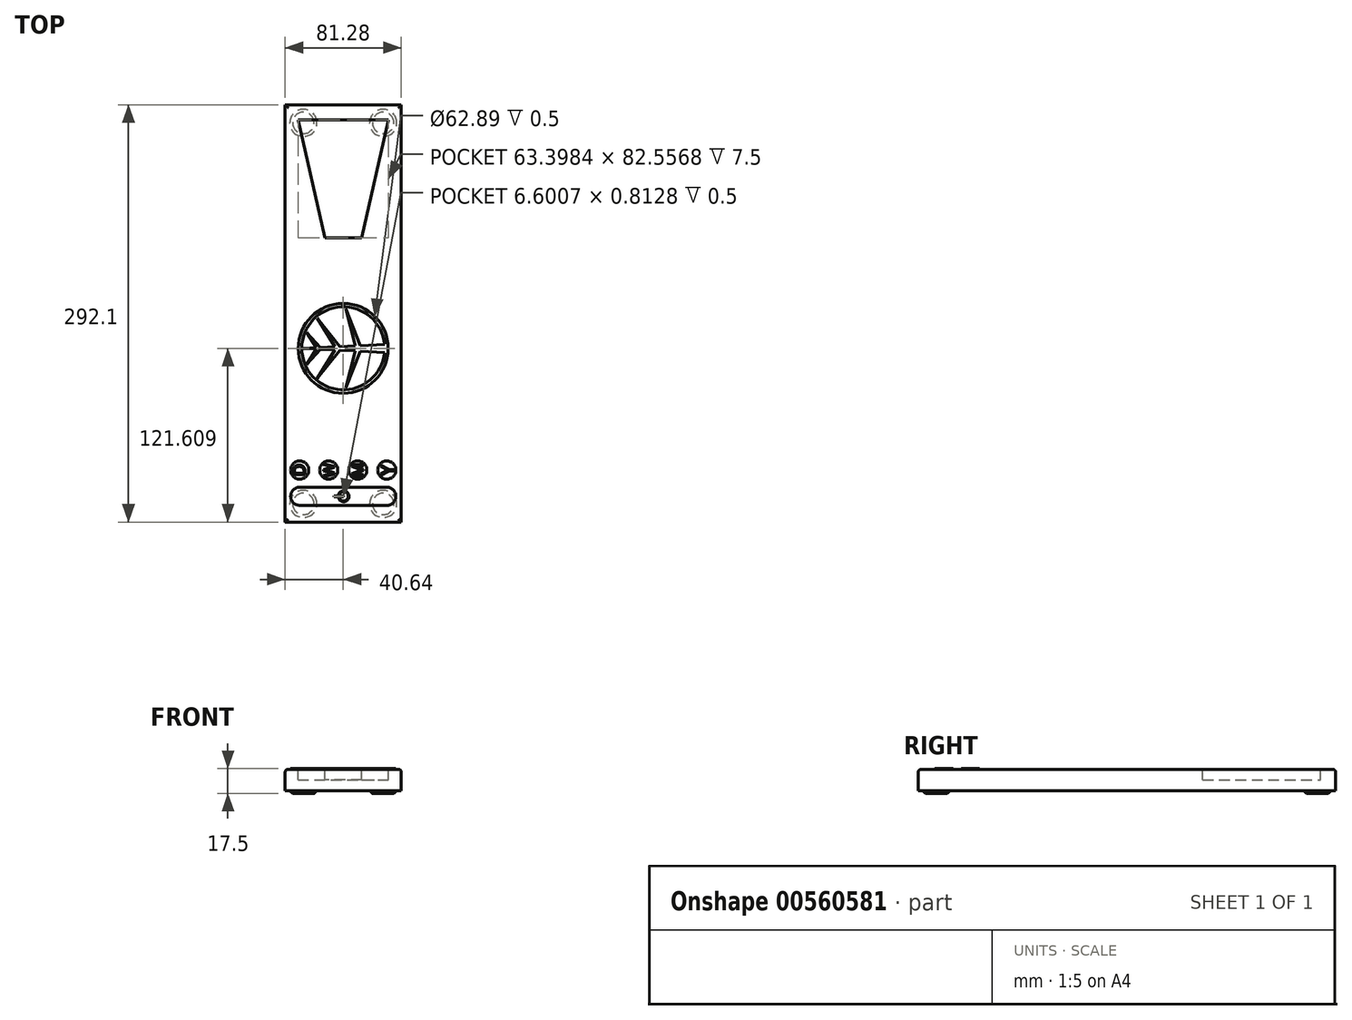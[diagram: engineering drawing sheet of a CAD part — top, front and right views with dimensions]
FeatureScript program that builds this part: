
annotation { "Feature Type Name" : "Feature", "Feature Type Description" : "" }
export const myFeature = defineFeature(function(context is Context, id is Id, definition is map)
    precondition{}
    {
        {
            var Q0;
            Q0=qCreatedBy(makeId("Right.planeOp"),FACE);
            var sketch = newSketch(context, id + "F0", { "sketchPlane" : qUnion([Q0])});
            skLineSegment(sketch, "E0.bottom", {"start": v(-151.29, 3.86) * mm, "end": v(140.81, 3.86) * mm});
            skLineSegment(sketch, "E0.top", {"start": v(-151.29, -11.14) * mm, "end": v(140.81, -11.14) * mm});
            skLineSegment(sketch, "E0.left", {"start": v(-151.29, 3.86) * mm, "end": v(-151.29, -11.14) * mm});
            skLineSegment(sketch, "E0.right", {"start": v(140.81, 3.86) * mm, "end": v(140.81, -11.14) * mm});
            skSolve(sketch);
        }
        {
            var Q0;
            Q0=makeQuery(id+"F0.imprint","IMPRINT",FACE,{"disambiguationData":[TD([[makeQuery(id+"F0.imprint","IMPRINT",EDGE,{"derivedFrom":sQuery(id+"F0.wireOp",EDGE,"E0.bottom")}),-1.0]])]});
            extrude(context, id + "F1", {"entities" : qUnion([Q0]), "depth" : 81.28 * mm, "offsetDistance" : 25.4 * mm});
        }
        {
            var Q0;
            Q0=makeQuery(id+"F1.opExtrude","SWEPT_FACE",FACE,{"disambiguationData":[OSD([sQuery(id+"F0.wireOp",EDGE,"E0.bottom")])]});
            var sketch = newSketch(context, id + "F2", { "sketchPlane" : qUnion([Q0])});
            skLineSegment(sketch, "E1", {"start": v(40.64, 130.27) * mm, "end": v(72.34, 130.27) * mm});
            skPoint(sketch, "E1.startSnap0", {"position": v(40.64, 140.81) * mm});
            skLineSegment(sketch, "E2", {"start": v(40.64, 130.27) * mm, "end": v(8.94, 130.27) * mm});
            skLineSegment(sketch, "E3", {"start": v(40.64, 47.71) * mm, "end": v(27.69, 47.71) * mm});
            skLineSegment(sketch, "E4", {"start": v(27.69, 47.71) * mm, "end": v(40.64, 47.71) * mm});
            skLineSegment(sketch, "E5", {"start": v(53.6, 47.71) * mm, "end": v(40.64, 47.71) * mm});
            skLineSegment(sketch, "E6", {"start": v(53.6, 47.71) * mm, "end": v(72.34, 130.27) * mm});
            skLineSegment(sketch, "E7", {"start": v(8.94, 130.27) * mm, "end": v(27.69, 47.71) * mm});
            skSolve(sketch);
        }
        {
            var Q0;
            Q0=makeQuery(id+"F2.imprint","IMPRINT",FACE,{"disambiguationData":[TD([[makeQuery(id+"F2.imprint","IMPRINT",EDGE,{"derivedFrom":sQuery(id+"F2.wireOp",EDGE,"E1")}),-1.0]])]});
            extrude(context, id + "F3", {"entities" : qUnion([Q0]), "operationType" : NewBodyOperationType.REMOVE, "oppositeDirection" : true, "depth" : 7.5 * mm, "offsetDistance" : 25.4 * mm});
        }
        {
            var Q0;
            Q0=makeQuery(id+"F1.opExtrude","SWEPT_FACE",FACE,{"disambiguationData":[OSD([sQuery(id+"F0.wireOp",EDGE,"E0.bottom")])]});
            var sketch = newSketch(context, id + "F4", { "sketchPlane" : qUnion([Q0])});
            skCircle(sketch, "E8", {"center": v(10.16, -114.9) * mm, "radius": 6.35 * mm});
            skCircle(sketch, "E9", {"center": v(30.48, -114.9) * mm, "radius": 6.35 * mm});
            skCircle(sketch, "E10", {"center": v(50.8, -114.9) * mm, "radius": 6.35 * mm});
            skCircle(sketch, "E11", {"center": v(71.12, -114.9) * mm, "radius": 6.35 * mm});
            skLineSegment(sketch, "E12", {"start": v(10.16, -114.9) * mm, "end": v(30.48, -114.9) * mm, "construction": true});
            skLineSegment(sketch, "E13", {"start": v(71.12, -114.9) * mm, "end": v(50.8, -114.9) * mm, "construction": true});
            skLineSegment(sketch, "E14", {"start": v(30.48, -114.9) * mm, "end": v(50.8, -114.9) * mm, "construction": true});
            skLineSegment(sketch, "E15.bottom", {"start": v(10.27, -126.9) * mm, "end": v(71.48, -126.9) * mm});
            skLineSegment(sketch, "E15.top", {"start": v(10.68, -139.58) * mm, "end": v(71.5, -139.58) * mm});
            skArc(sketch, "E16", {"start": v(10.27, -126.9) * mm, "mid": v(3.81, -133.45) * mm, "end": v(10.68, -139.58) * mm});
            skArc(sketch, "E17", {"start": v(71.5, -139.58) * mm, "mid": v(77.47, -133.23) * mm, "end": v(71.48, -126.9) * mm});
            skSolve(sketch);
        }
        {
            var Q0;
            Q0 = qSketchRegion(id + "F4", true);
            extrude(context, id + "F5", {"entities" : qUnion([Q0]), "operationType" : NewBodyOperationType.ADD, "depth" : .5 * mm, "offsetDistance" : 25.4 * mm});
        }
        {
            var Q0;
            Q0=makeQuery(id+"F5.opExtrude","CAP_FACE",FACE,{"disambiguationData":[OSD([sQuery(id+"F4.wireOp",EDGE,"E8")])],"isStart":false});
            var sketch = newSketch(context, id + "F6", { "sketchPlane" : qUnion([Q0])});
            skText(sketch, "E18", { "text": "D", "fontName": "OpenSans-Regular.ttf"});
            const initialGuessF6  = {"E18": [0.01393, -0.11922, 0, 1, 0.00842]};
            skSetInitialGuess(sketch, initialGuessF6);
            skSolve(sketch);
        }
        {
            var Q0;
            Q0 = qSketchRegion(id + "F6", true);
            extrude(context, id + "F7", {"entities" : qUnion([Q0]), "operationType" : NewBodyOperationType.REMOVE, "oppositeDirection" : true, "depth" : .5 * mm, "offsetDistance" : 25.4 * mm});
        }
        {
            var Q0;
            Q0=makeQuery(id+"F5.opExtrude","CAP_FACE",FACE,{"disambiguationData":[OSD([sQuery(id+"F4.wireOp",EDGE,"E9")])],"isStart":false});
            var sketch = newSketch(context, id + "F8", { "sketchPlane" : qUnion([Q0])});
            skText(sketch, "E19", { "text": "W", "fontName": "OpenSans-Regular.ttf"});
            const initialGuessF8  = {"E19": [0.03434, -0.1197, 0, 1, 0.00744]};
            skSetInitialGuess(sketch, initialGuessF8);
            skSolve(sketch);
        }
        {
            var Q0;
            Q0 = qSketchRegion(id + "F8", true);
            extrude(context, id + "F9", {"entities" : qUnion([Q0]), "operationType" : NewBodyOperationType.REMOVE, "oppositeDirection" : true, "depth" : .5 * mm, "offsetDistance" : 25.4 * mm});
        }
        {
            var Q0;
            Q0=makeQuery(id+"F5.opExtrude","CAP_FACE",FACE,{"disambiguationData":[OSD([sQuery(id+"F4.wireOp",EDGE,"E10")])],"isStart":false});
            var sketch = newSketch(context, id + "F10", { "sketchPlane" : qUnion([Q0])});
            skText(sketch, "E20", { "text": "M", "fontName": "OpenSans-Regular.ttf"});
            const initialGuessF10  = {"E20": [0.05468, -0.11996, 0, 1, 0.00807]};
            skSetInitialGuess(sketch, initialGuessF10);
            skSolve(sketch);
        }
        {
            var Q0;
            Q0 = qSketchRegion(id + "F10", true);
            extrude(context, id + "F11", {"entities" : qUnion([Q0]), "operationType" : NewBodyOperationType.REMOVE, "oppositeDirection" : true, "depth" : .5 * mm, "offsetDistance" : 25.4 * mm});
        }
        {
            var Q0;
            Q0=makeQuery(id+"F5.opExtrude","CAP_FACE",FACE,{"disambiguationData":[OSD([sQuery(id+"F4.wireOp",EDGE,"E11")])],"isStart":false});
            var sketch = newSketch(context, id + "F12", { "sketchPlane" : qUnion([Q0])});
            skText(sketch, "E21", { "text": "Y", "fontName": "OpenSans-Regular.ttf"});
            const initialGuessF12  = {"E21": [0.07649, -0.1187, 0, 1, 0.00957]};
            skSetInitialGuess(sketch, initialGuessF12);
            skSolve(sketch);
        }
        {
            var Q0;
            Q0 = qSketchRegion(id + "F12", true);
            extrude(context, id + "F13", {"entities" : qUnion([Q0]), "operationType" : NewBodyOperationType.REMOVE, "oppositeDirection" : true, "depth" : .5 * mm, "offsetDistance" : 25.4 * mm});
        }
        {
            var Q0;
            Q0=makeQuery(id+"F5.opExtrude","CAP_FACE",FACE,{"disambiguationData":[OSD([sQuery(id+"F4.wireOp",EDGE,"E15.bottom"),sQuery(id+"F4.wireOp",EDGE,"E15.top"),sQuery(id+"F4.wireOp",EDGE,"E16"),sQuery(id+"F4.wireOp",EDGE,"E17")])],"isStart":false});
            var sketch = newSketch(context, id + "F14", { "sketchPlane" : qUnion([Q0])});
            skArc(sketch, "E22", {"start": v(37.35, -134.68) * mm, "mid": v(44.68, -133.17) * mm, "end": v(37.3, -131.93) * mm});
            skPoint(sketch, "E23", {"position": v(40.87, -126.9) * mm});
            skArc(sketch, "E24", {"start": v(37.87, -134.46) * mm, "mid": v(44.12, -133.18) * mm, "end": v(37.83, -132.13) * mm});
            skLineSegment(sketch, "E25", {"start": v(37.3, -131.93) * mm, "end": v(37.83, -132.13) * mm});
            skLineSegment(sketch, "E26", {"start": v(37.35, -134.68) * mm, "end": v(37.87, -134.46) * mm});
            skLineSegment(sketch, "E27.bottom", {"start": v(40.87, -132.89) * mm, "end": v(34.27, -132.89) * mm});
            skLineSegment(sketch, "E27.top", {"start": v(40.87, -133.7) * mm, "end": v(34.27, -133.7) * mm});
            skLineSegment(sketch, "E27.left", {"start": v(40.87, -132.89) * mm, "end": v(40.87, -133.7) * mm});
            skLineSegment(sketch, "E27.right", {"start": v(34.27, -132.89) * mm, "end": v(34.27, -133.7) * mm});
            skPoint(sketch, "E27.middle", {"position": v(37.57, -133.3) * mm});
            skPoint(sketch, "E28.orphan", {"position": v(34.27, -133.35) * mm});
            skSolve(sketch);
        }
        {
            var Q0;
            Q0=makeQuery(id+"F14.imprint","IMPRINT",FACE,{"disambiguationData":[TD([[makeQuery(id+"F14.imprint","IMPRINT",EDGE,{"derivedFrom":sQuery(id+"F14.wireOp",EDGE,"E22")}),1.0]])]});
            var Q1;
            Q1=makeQuery(id+"F14.imprint","IMPRINT",FACE,{"disambiguationData":[TD([[makeQuery(id+"F14.imprint","IMPRINT",EDGE,{"derivedFrom":sQuery(id+"F14.wireOp",EDGE,"E27.bottom")}),1.0]])]});
            extrude(context, id + "F15", {"entities" : qUnion([Q0, Q1]), "operationType" : NewBodyOperationType.REMOVE, "oppositeDirection" : true, "depth" : .5 * mm, "offsetDistance" : 25.4 * mm});
        }
        {
            var Q0;
            Q0=makeQuery(id+"F1.opExtrude","SWEPT_FACE",FACE,{"disambiguationData":[OSD([sQuery(id+"F0.wireOp",EDGE,"E0.bottom")])]});
            var sketch = newSketch(context, id + "F16", { "sketchPlane" : qUnion([Q0])});
            skPoint(sketch, "E29.centerSnap0", {"position": v(40.64, 47.71) * mm});
            skLineSegment(sketch, "E30", {"start": v(69.57, -26.9) * mm, "end": v(52.44, -27.73) * mm});
            skLineSegment(sketch, "E31", {"start": v(48.98, -27.9) * mm, "end": v(42.32, -1.92) * mm});
            skLineSegment(sketch, "E32", {"start": v(42.32, -1.92) * mm, "end": v(52.44, -27.73) * mm});
            skLineSegment(sketch, "E33", {"start": v(34.8, -28.6) * mm, "end": v(22.47, -8.64) * mm});
            skLineSegment(sketch, "E34", {"start": v(22.47, -8.64) * mm, "end": v(38.35, -28.43) * mm});
            skLineSegment(sketch, "E35", {"start": v(24.67, -29.1) * mm, "end": v(15.13, -18.62) * mm});
            skPoint(sketch, "E35.endSnap0", {"position": v(28.63, -18.62) * mm});
            skLineSegment(sketch, "E36", {"start": v(15.13, -18.62) * mm, "end": v(21.7, -29.25) * mm});
            skLineSegment(sketch, "E37.trimOffspring", {"start": v(48.98, -27.9) * mm, "end": v(38.35, -28.43) * mm});
            skLineSegment(sketch, "E38.trimOffspring", {"start": v(34.8, -28.6) * mm, "end": v(24.67, -29.1) * mm});
            skLineSegment(sketch, "E39.trimOffspring", {"start": v(21.7, -29.25) * mm, "end": v(12.83, -29.68) * mm});
            skPoint(sketch, "E40.MirrorP", {"position": v(28.63, -40.74) * mm});
            skLineSegment(sketch, "E41.MirrorCS", {"start": v(21.7, -30.12) * mm, "end": v(12.83, -29.68) * mm});
            skLineSegment(sketch, "E42.MirrorCS", {"start": v(48.98, -31.46) * mm, "end": v(38.35, -30.94) * mm});
            skLineSegment(sketch, "E43.MirrorCS", {"start": v(22.47, -50.73) * mm, "end": v(38.35, -30.94) * mm});
            skLineSegment(sketch, "E44.MirrorCS", {"start": v(34.8, -30.76) * mm, "end": v(24.67, -30.26) * mm});
            skLineSegment(sketch, "E45.MirrorCS", {"start": v(15.13, -40.74) * mm, "end": v(21.7, -30.12) * mm});
            skLineSegment(sketch, "E46.MirrorCS", {"start": v(24.67, -30.26) * mm, "end": v(15.13, -40.74) * mm});
            skLineSegment(sketch, "E47.MirrorCS", {"start": v(42.32, -57.44) * mm, "end": v(52.44, -31.63) * mm});
            skLineSegment(sketch, "E48.MirrorCS", {"start": v(69.55, -32.67) * mm, "end": v(52.44, -31.63) * mm});
            skLineSegment(sketch, "E49.MirrorCS", {"start": v(48.98, -31.46) * mm, "end": v(42.32, -57.44) * mm});
            skLineSegment(sketch, "E50.MirrorCS", {"start": v(34.8, -30.76) * mm, "end": v(22.47, -50.73) * mm});
            skArc(sketch, "E51", {"start": v(69.57, -26.9) * mm, "mid": v(11.58, -29.58) * mm, "end": v(69.55, -32.67) * mm});
            skCircle(sketch, "E52", {"center": v(40.64, -29.68) * mm, "radius": 31.44 * mm});
            skSolve(sketch);
        }
        {
            var Q0;
            Q0 = qSketchRegion(id + "F16", true);
            extrude(context, id + "F17", {"entities" : qUnion([Q0]), "operationType" : NewBodyOperationType.REMOVE, "oppositeDirection" : true, "depth" : .5 * mm, "offsetDistance" : 25.4 * mm});
        }
        {
            var Q0;
            Q0=makeQuery(id+"F1.opExtrude","CAP_EDGE",EDGE,{"disambiguationData":[OSD([sQuery(id+"F0.wireOp",EDGE,"E0.bottom")])],"isStart":false});
            var Q1;
            Q1=makeQuery(id+"F1.opExtrude","SWEPT_EDGE",EDGE,{"disambiguationData":[OSD([sQuery(id+"F0.wireOp",EDGE,"E0.bottom"),sQuery(id+"F0.wireOp",EDGE,"E0.left")])]});
            var Q2;
            Q2=makeQuery(id+"F1.opExtrude","CAP_EDGE",EDGE,{"disambiguationData":[OSD([sQuery(id+"F0.wireOp",EDGE,"E0.bottom")])],"isStart":true});
            var Q3;
            Q3=makeQuery(id+"F1.opExtrude","SWEPT_EDGE",EDGE,{"disambiguationData":[OSD([sQuery(id+"F0.wireOp",EDGE,"E0.bottom"),sQuery(id+"F0.wireOp",EDGE,"E0.right")])]});
            fillet(context, id + "F18", {"entities" : qUnion([Q0, Q1, Q2, Q3]), "radius" : 2 * mm, "tangentPropagation" : true, "allowEdgeOverflow" : false});
        }
        {
            var Q0;
            Q0=makeQuery(id+"F1.opExtrude","SWEPT_FACE",FACE,{"disambiguationData":[OSD([sQuery(id+"F0.wireOp",EDGE,"E0.top")])]});
            var sketch = newSketch(context, id + "F19", { "sketchPlane" : qUnion([Q0])});
            skCircle(sketch, "E53", {"center": v(68.58, 138.59) * mm, "radius": 9.53 * mm});
            skCircle(sketch, "E54", {"center": v(12.7, 138.59) * mm, "radius": 9.53 * mm});
            skCircle(sketch, "E55", {"center": v(68.58, -128.11) * mm, "radius": 9.53 * mm});
            skCircle(sketch, "E56", {"center": v(12.7, -128.11) * mm, "radius": 9.53 * mm});
            skSolve(sketch);
        }
        {
            var Q0;
            Q0 = qSketchRegion(id + "F19", true);
            extrude(context, id + "F20", {"entities" : qUnion([Q0]), "operationType" : NewBodyOperationType.ADD, "depth" : 2 * mm, "offsetDistance" : 25.4 * mm});
        }
        {
            var Q0;
            Q0=makeQuery(id+"F20.opExtrude","CAP_EDGE",EDGE,{"disambiguationData":[OSD([sQuery(id+"F19.wireOp",EDGE,"E53")])],"isStart":false});
            var Q1;
            Q1=makeQuery(id+"F20.opExtrude","CAP_EDGE",EDGE,{"disambiguationData":[OSD([sQuery(id+"F19.wireOp",EDGE,"E54")])],"isStart":false});
            var Q2;
            Q2=makeQuery(id+"F20.opExtrude","CAP_EDGE",EDGE,{"disambiguationData":[OSD([sQuery(id+"F19.wireOp",EDGE,"E55")])],"isStart":false});
            var Q3;
            Q3=makeQuery(id+"F20.opExtrude","CAP_EDGE",EDGE,{"disambiguationData":[OSD([sQuery(id+"F19.wireOp",EDGE,"E56")])],"isStart":false});
            chamfer(context, id + "F21", {"entities" : qUnion([Q0, Q1, Q2, Q3]), "width" : 2 * mm, "tangentPropagation" : true});
        }
    });
